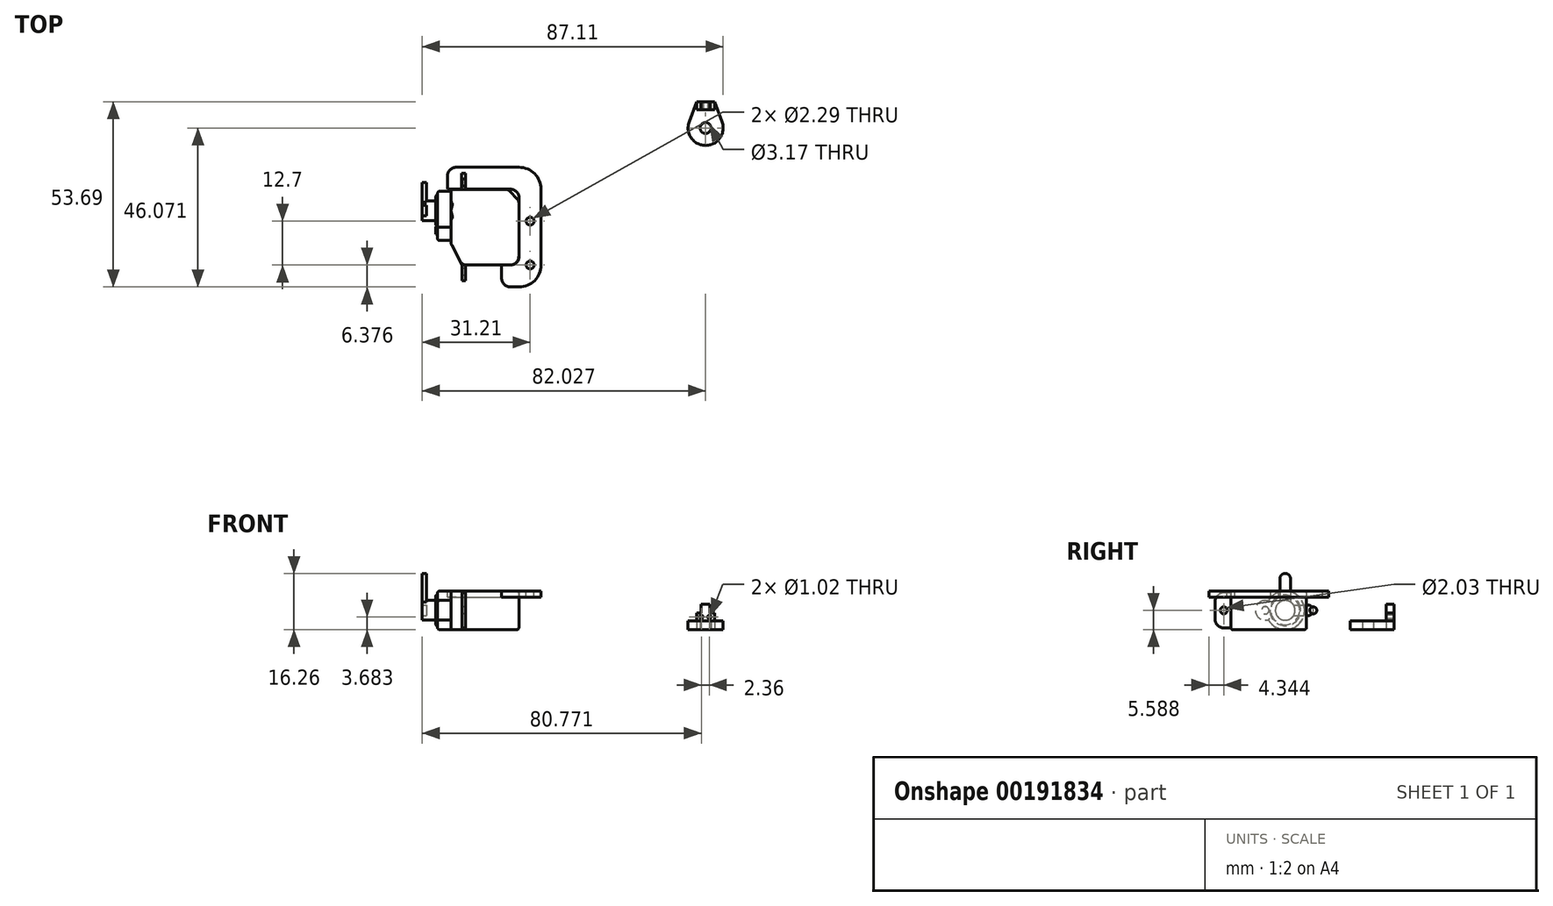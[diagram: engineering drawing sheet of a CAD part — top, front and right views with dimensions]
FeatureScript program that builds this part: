
annotation { "Feature Type Name" : "Feature", "Feature Type Description" : "" }
export const myFeature = defineFeature(function(context is Context, id is Id, definition is map)
    precondition{}
    {
        {
            var Q0;
            Q0=qCreatedBy(makeId("Top.planeOp"),FACE);
            var sketch = newSketch(context, id + "F0", { "sketchPlane" : qUnion([Q0])});
            skLineSegment(sketch, "E0.top", {"start": v(-31.68, -0.42) * mm, "end": v(-18.72, -0.42) * mm});
            skLineSegment(sketch, "E0.left", {"start": v(-35.87, 22.38) * mm, "end": v(-35.87, 6.41) * mm});
            skLineSegment(sketch, "E0.right", {"start": v(-16.18, 17.68) * mm, "end": v(-16.18, 2.12) * mm});
            skLineSegment(sketch, "E1", {"start": v(-32.7, -0.42) * mm, "end": v(-35.59, 5.26) * mm});
            skLineSegment(sketch, "E2.top", {"start": v(-32.7, -5) * mm, "end": v(-31.68, -5) * mm});
            skLineSegment(sketch, "E2.left", {"start": v(-32.7, -0.42) * mm, "end": v(-32.7, -5) * mm});
            skLineSegment(sketch, "E2.right", {"start": v(-31.68, -0.42) * mm, "end": v(-31.68, -5) * mm});
            skPoint(sketch, "E3.visualSharp", {"position": v(-17.03, 21.42) * mm});
            skPoint(sketch, "E4.visualSharp", {"position": v(-16.18, 22.74) * mm});
            skPoint(sketch, "E5.visualSharp", {"position": v(-16.18, -0.42) * mm});
            skArc(sketch, "E5.filletArc", {"start": v(-18.72, -0.42) * mm, "mid": v(-16.93, 0.32) * mm, "end": v(-16.18, 2.12) * mm});
            skPoint(sketch, "E6.visualSharp", {"position": v(-35.87, 5.8) * mm});
            skArc(sketch, "E6.filletArc", {"start": v(-35.87, 6.41) * mm, "mid": v(-35.8, 5.82) * mm, "end": v(-35.59, 5.26) * mm});
            skLineSegment(sketch, "E7", {"start": v(-43.65, 10.5) * mm, "end": v(-4.37, 10.5) * mm, "construction": true});
            skLineSegment(sketch, "E8.MirrorCS", {"start": v(-31.68, 21.42) * mm, "end": v(-31.68, 26) * mm});
            skLineSegment(sketch, "E9.MirrorCS", {"start": v(-32.7, 21.42) * mm, "end": v(-32.7, 26) * mm});
            skLineSegment(sketch, "E10.MirrorCS", {"start": v(-32.7, 26) * mm, "end": v(-31.68, 26) * mm});
            skLineSegment(sketch, "E11.trimOffspring", {"start": v(-31.68, 21.42) * mm, "end": v(-19.8, 21.42) * mm});
            skLineSegment(sketch, "E12", {"start": v(-32.7, 21.42) * mm, "end": v(-33.48, 21.42) * mm});
            skLineSegment(sketch, "E13", {"start": v(-33.48, 21.42) * mm, "end": v(-35.36, 21.42) * mm});
            skLineSegment(sketch, "E14", {"start": v(-35.87, 22.38) * mm, "end": v(-35.87, 20.91) * mm});
            skPoint(sketch, "E15.visualSharp", {"position": v(-35.87, 21.42) * mm});
            skArc(sketch, "E15.filletArc", {"start": v(-35.36, 21.42) * mm, "mid": v(-35.72, 21.27) * mm, "end": v(-35.87, 20.91) * mm});
            skLineSegment(sketch, "E16", {"start": v(-18.88, 21.03) * mm, "end": v(-16.53, 18.56) * mm});
            skPoint(sketch, "E17.visualSharp", {"position": v(-19.26, 21.42) * mm});
            skArc(sketch, "E17.filletArc", {"start": v(-18.88, 21.03) * mm, "mid": v(-19.3, 21.32) * mm, "end": v(-19.8, 21.42) * mm});
            skPoint(sketch, "E18.visualSharp", {"position": v(-16.18, 18.2) * mm});
            skArc(sketch, "E18.filletArc", {"start": v(-16.18, 17.68) * mm, "mid": v(-16.27, 18.15) * mm, "end": v(-16.53, 18.56) * mm});
            skSolve(sketch);
        }
        {
            var Q0;
            Q0=makeQuery(id+"F0.imprint","IMPRINT",FACE,{"disambiguationData":[TD([[makeQuery(id+"F0.imprint","IMPRINT",EDGE,{"derivedFrom":sQuery(id+"F0.wireOp",EDGE,"E0.top")}),1.0]])]});
            extrude(context, id + "F1", {"entities" : qUnion([Q0]), "depth" : 11.18 * mm});
        }
        {
            var Q0;
            Q0=makeQuery(id+"F1.opExtrude","SWEPT_FACE",FACE,{"disambiguationData":[OSD([sQuery(id+"F0.wireOp",EDGE,"E0.left")])]});
            var sketch = newSketch(context, id + "F2", { "sketchPlane" : qUnion([Q0])});
            skArc(sketch, "E19", {"start": v(-10.44, 8.3) * mm, "mid": v(-20.91, 5.59) * mm, "end": v(-10.44, 2.87) * mm});
            skLineSegment(sketch, "E20", {"start": v(-6.41, 5.59) * mm, "end": v(-20.91, 5.59) * mm, "construction": true});
            skArc(sketch, "E21", {"start": v(-10.44, 2.87) * mm, "mid": v(-6.7, 5.59) * mm, "end": v(-10.44, 8.3) * mm});
            skLineSegment(sketch, "E22", {"start": v(-9.55, 2.73) * mm, "end": v(-10.52, 2.73) * mm});
            skLineSegment(sketch, "E23", {"start": v(-9.55, 8.45) * mm, "end": v(-10.52, 8.45) * mm});
            skSolve(sketch);
        }
        {
            var Q0;
            Q0 = qSketchRegion(id + "F2", true);
            extrude(context, id + "F3", {"entities" : qUnion([Q0]), "operationType" : NewBodyOperationType.ADD, "depth" : 3.8 * mm});
        }
        {
            var Q0;
            Q0=makeQuery(id+"F3.opExtrude","CAP_FACE",FACE,{"disambiguationData":[OSD([sQuery(id+"F2.wireOp",EDGE,"E19"),sQuery(id+"F2.wireOp",EDGE,"E21"),sQuery(id+"F2.wireOp",EDGE,"E22"),sQuery(id+"F2.wireOp",EDGE,"E23")])],"isStart":false});
            fillet(context, id + "F4", {"entities" : qUnion([Q0]), "radius" : 0.5 * mm, "tangentPropagation" : true, "allowEdgeOverflow" : false});
        }
        {
            var Q0;
            Q0=makeQuery(id+"F3.opExtrude","CAP_FACE",FACE,{"disambiguationData":[OSD([sQuery(id+"F2.wireOp",EDGE,"E19"),sQuery(id+"F2.wireOp",EDGE,"E21"),sQuery(id+"F2.wireOp",EDGE,"E22"),sQuery(id+"F2.wireOp",EDGE,"E23")])],"isStart":false});
            var sketch = newSketch(context, id + "F5", { "sketchPlane" : qUnion([Q0])});
            skCircle(sketch, "E24", {"center": v(-15.33, 5.59) * mm, "radius": 4.45 * mm});
            skCircle(sketch, "E25", {"center": v(-9.55, 5.59) * mm, "radius": 1.08 * mm});
            skSolve(sketch);
        }
        {
            var Q0;
            Q0 = qSketchRegion(id + "F5", true);
            extrude(context, id + "F6", {"entities" : qUnion([Q0]), "operationType" : NewBodyOperationType.ADD, "depth" : 0.64 * mm});
        }
        {
            var Q0;
            Q0=makeQuery(id+"F6.opExtrude","CAP_FACE",FACE,{"disambiguationData":[OSD([sQuery(id+"F5.wireOp",EDGE,"E24")])],"isStart":false});
            chamfer(context, id + "F7", {"entities" : qUnion([Q0]), "width" : 0.25 * mm, "tangentPropagation" : true});
        }
        {
            var Q0;
            Q0=makeQuery(id+"F1.opExtrude","SWEPT_FACE",FACE,{"disambiguationData":[OSD([sQuery(id+"F0.wireOp",EDGE,"E2.left")])]});
            var sketch = newSketch(context, id + "F8", { "sketchPlane" : qUnion([Q0])});
            skLineSegment(sketch, "E26.bottom", {"start": v(0.42, 0.5) * mm, "end": v(2.46, 0.5) * mm});
            skLineSegment(sketch, "E26.top", {"start": v(0.42, 10.67) * mm, "end": v(2.46, 10.67) * mm});
            skLineSegment(sketch, "E26.left", {"start": v(0.42, 0.5) * mm, "end": v(0.42, 10.67) * mm});
            skLineSegment(sketch, "E26.right", {"start": v(5, 3.05) * mm, "end": v(5, 8.13) * mm});
            skPoint(sketch, "E27.visualSharp", {"position": v(5, 0.5) * mm});
            skArc(sketch, "E27.filletArc", {"start": v(2.46, 0.5) * mm, "mid": v(4.25, 1.25) * mm, "end": v(5, 3.05) * mm});
            skPoint(sketch, "E28.visualSharp", {"position": v(5, 10.67) * mm});
            skArc(sketch, "E28.filletArc", {"start": v(5, 8.13) * mm, "mid": v(4.25, 9.92) * mm, "end": v(2.46, 10.67) * mm});
            skCircle(sketch, "E29", {"center": v(2.46, 5.59) * mm, "radius": 1.02 * mm});
            skLineSegment(sketch, "E30", {"start": v(0.42, 5.59) * mm, "end": v(5, 5.59) * mm, "construction": true});
            skLineSegment(sketch, "E31", {"start": v(-10.5, -16.54) * mm, "end": v(-10.5, 30.53) * mm, "construction": true});
            skLineSegment(sketch, "E32.MirrorCS", {"start": v(-21.42, 10.67) * mm, "end": v(-23.45, 10.67) * mm});
            skLineSegment(sketch, "E33.MirrorCS", {"start": v(-21.42, 0.5) * mm, "end": v(-23.45, 0.5) * mm});
            skArc(sketch, "E34.MirrorCS", {"start": v(-23.45, 0.5) * mm, "mid": v(-25.25, 1.25) * mm, "end": v(-26, 3.05) * mm});
            skLineSegment(sketch, "E35.MirrorCS", {"start": v(-21.42, 5.59) * mm, "end": v(-26, 5.59) * mm, "construction": true});
            skLineSegment(sketch, "E36.MirrorCS", {"start": v(-26, 3.05) * mm, "end": v(-26, 8.13) * mm});
            skArc(sketch, "E37.MirrorCS", {"start": v(-26, 8.13) * mm, "mid": v(-25.25, 9.92) * mm, "end": v(-23.45, 10.67) * mm});
            skCircle(sketch, "E38.MirrorC", {"center": v(-23.45, 5.59) * mm, "radius": 1.02 * mm});
            skPoint(sketch, "E39.MirrorP", {"position": v(-26, 10.67) * mm});
            skLineSegment(sketch, "E40.MirrorCS", {"start": v(-21.42, 0.5) * mm, "end": v(-21.42, 10.67) * mm});
            skPoint(sketch, "E41.MirrorP", {"position": v(-26, 0.5) * mm});
            skLineSegment(sketch, "E42.bottom", {"start": v(-21.42, 0) * mm, "end": v(-26, 0) * mm});
            skLineSegment(sketch, "E42.top", {"start": v(-21.42, 11.2) * mm, "end": v(-26, 11.2) * mm});
            skLineSegment(sketch, "E42.left", {"start": v(-21.42, 0) * mm, "end": v(-21.42, 11.2) * mm});
            skLineSegment(sketch, "E42.right", {"start": v(-26, 0) * mm, "end": v(-26, 11.2) * mm});
            skSolve(sketch);
        }
        {
            var Q0;
            Q0=makeQuery(id+"F8.imprint","IMPRINT",FACE,{"disambiguationData":[TD([[makeQuery(id+"F8.imprint","IMPRINT",EDGE,{"derivedFrom":sQuery(id+"F8.wireOp",EDGE,"E29")}),1.0]])]});
            var Q1;
            {var subQ0=sQuery(id+"F8.wireOp",EDGE,"E28.filletArc");Q1=makeQuery(id+"F8.imprint","IMPRINT",FACE,{"disambiguationData":[TD([[makeQuery(id+"F8.imprint","IMPRINT",EDGE,{"derivedFrom":subQ0}),-1.0]])]});}
            var Q2;
            {var subQ0=sQuery(id+"F8.wireOp",EDGE,"E27.filletArc");Q2=makeQuery(id+"F8.imprint","IMPRINT",FACE,{"disambiguationData":[TD([[makeQuery(id+"F8.imprint","IMPRINT",EDGE,{"derivedFrom":subQ0}),-1.0]])]});}
            var Q3;
            {var subQ1=sQuery(id+"F8.wireOp",EDGE,"E32.MirrorCS");Q3=makeQuery(id+"F8.imprint","IMPRINT",FACE,{"disambiguationData":[TD([[makeQuery(id+"F8.imprint","IMPRINT",EDGE,{"derivedFrom":subQ1}),-1.0]])]});}
            var Q4;
            {var subQ1=sQuery(id+"F8.wireOp",EDGE,"E33.MirrorCS");Q4=makeQuery(id+"F8.imprint","IMPRINT",FACE,{"disambiguationData":[TD([[makeQuery(id+"F8.imprint","IMPRINT",EDGE,{"derivedFrom":subQ1}),1.0]])]});}
            var Q5;
            Q5=makeQuery(id+"F8.imprint","IMPRINT",FACE,{"disambiguationData":[TD([[makeQuery(id+"F8.imprint","IMPRINT",EDGE,{"derivedFrom":sQuery(id+"F8.wireOp",EDGE,"E38.MirrorC")}),-1.0]])]});
            extrude(context, id + "F9", {"entities" : qUnion([Q0, Q1, Q2, Q3, Q4, Q5]), "operationType" : NewBodyOperationType.REMOVE, "endBound" : BoundingType.THROUGH_ALL, "oppositeDirection" : true, "depth" : 25.4 * mm});
        }
        {
            var Q0;
            Q0=makeQuery(id+"F1.opExtrude","CAP_FACE",FACE,{"disambiguationData":[OSD([sQuery(id+"F0.wireOp",EDGE,"E0.top"),sQuery(id+"F0.wireOp",EDGE,"E0.left"),sQuery(id+"F0.wireOp",EDGE,"E0.right"),sQuery(id+"F0.wireOp",EDGE,"0QajpKrW-Zkmi-OHnB-r6oI-nad7adF06jMD"),sQuery(id+"F0.wireOp",EDGE,"E1"),sQuery(id+"F0.wireOp",EDGE,"E2.top"),sQuery(id+"F0.wireOp",EDGE,"E2.left"),sQuery(id+"F0.wireOp",EDGE,"E2.right"),sQuery(id+"F0.wireOp",EDGE,"E3.filletArc"),sQuery(id+"F0.wireOp",EDGE,"E4.filletArc"),sQuery(id+"F0.wireOp",EDGE,"E5.filletArc"),sQuery(id+"F0.wireOp",EDGE,"E6.filletArc"),sQuery(id+"F0.wireOp",EDGE,"E8.MirrorCS"),sQuery(id+"F0.wireOp",EDGE,"E9.MirrorCS"),sQuery(id+"F0.wireOp",EDGE,"E10.MirrorCS"),sQuery(id+"F0.wireOp",EDGE,"E11.trimOffspring"),sQuery(id+"F0.wireOp",EDGE,"E12"),sQuery(id+"F0.wireOp",EDGE,"E13"),sQuery(id+"F0.wireOp",EDGE,"E14"),sQuery(id+"F0.wireOp",EDGE,"E15.filletArc")])],"isStart":false});
            var Q1;
            Q1=makeQuery(id+"F1.opExtrude","CAP_FACE",FACE,{"disambiguationData":[OSD([sQuery(id+"F0.wireOp",EDGE,"E0.top"),sQuery(id+"F0.wireOp",EDGE,"E0.left"),sQuery(id+"F0.wireOp",EDGE,"E0.right"),sQuery(id+"F0.wireOp",EDGE,"0QajpKrW-Zkmi-OHnB-r6oI-nad7adF06jMD"),sQuery(id+"F0.wireOp",EDGE,"E1"),sQuery(id+"F0.wireOp",EDGE,"E2.top"),sQuery(id+"F0.wireOp",EDGE,"E2.left"),sQuery(id+"F0.wireOp",EDGE,"E2.right"),sQuery(id+"F0.wireOp",EDGE,"E3.filletArc"),sQuery(id+"F0.wireOp",EDGE,"E4.filletArc"),sQuery(id+"F0.wireOp",EDGE,"E5.filletArc"),sQuery(id+"F0.wireOp",EDGE,"E6.filletArc"),sQuery(id+"F0.wireOp",EDGE,"E8.MirrorCS"),sQuery(id+"F0.wireOp",EDGE,"E9.MirrorCS"),sQuery(id+"F0.wireOp",EDGE,"E10.MirrorCS"),sQuery(id+"F0.wireOp",EDGE,"E11.trimOffspring"),sQuery(id+"F0.wireOp",EDGE,"E12"),sQuery(id+"F0.wireOp",EDGE,"E13"),sQuery(id+"F0.wireOp",EDGE,"E14"),sQuery(id+"F0.wireOp",EDGE,"E15.filletArc")])],"isStart":true});
            fillet(context, id + "F10", {"entities" : qUnion([Q0, Q1]), "radius" : 0.5 * mm, "tangentPropagation" : true, "allowEdgeOverflow" : false});
        }
        {
            var Q0;
            Q0=makeQuery(id+"F6.opExtrude","CAP_FACE",FACE,{"disambiguationData":[OSD([sQuery(id+"F5.wireOp",EDGE,"E24")])],"isStart":false});
            var sketch = newSketch(context, id + "F11", { "sketchPlane" : qUnion([Q0])});
            skCircle(sketch, "E43", {"center": v(-15.33, 5.59) * mm, "radius": 2.86 * mm});
            skSolve(sketch);
        }
        {
            var Q0;
            Q0 = qSketchRegion(id + "F11", true);
            extrude(context, id + "F12", {"entities" : qUnion([Q0]), "depth" : 3.8 * mm});
        }
        {
            var Q0;
            Q0=qCreatedBy(makeId("Top.planeOp"),FACE);
            var sketch = newSketch(context, id + "F13", { "sketchPlane" : qUnion([Q0])});
            skArc(sketch, "E44", {"start": v(33.13, 41) * mm, "mid": v(37.9, 34.2) * mm, "end": v(42.68, 41) * mm});
            skLineSegment(sketch, "E45", {"start": v(33.13, 41) * mm, "end": v(35.27, 46.9) * mm});
            skLineSegment(sketch, "E46", {"start": v(35.27, 46.9) * mm, "end": v(36.64, 46.9) * mm});
            skLineSegment(sketch, "E47", {"start": v(40.54, 46.9) * mm, "end": v(42.68, 41) * mm});
            skCircle(sketch, "E48", {"center": v(37.9, 39.27) * mm, "radius": 1.59 * mm});
            skLineSegment(sketch, "E49", {"start": v(37.9, 39.27) * mm, "end": v(37.9, 46.9) * mm, "construction": true});
            skLineSegment(sketch, "E50.top", {"start": v(36.64, 44.6) * mm, "end": v(39.18, 44.6) * mm});
            skLineSegment(sketch, "E50.left", {"start": v(36.64, 46.9) * mm, "end": v(36.64, 44.6) * mm});
            skLineSegment(sketch, "E50.right", {"start": v(39.18, 46.9) * mm, "end": v(39.18, 44.6) * mm});
            skLineSegment(sketch, "E51.trimOffspring", {"start": v(39.18, 46.9) * mm, "end": v(40.54, 46.9) * mm});
            skSolve(sketch);
        }
        {
            var Q0;
            Q0=makeQuery(id+"F12.opExtrude","CAP_FACE",FACE,{"disambiguationData":[OSD([sQuery(id+"F11.wireOp",EDGE,"E43")])],"isStart":false});
            var sketch = newSketch(context, id + "F14", { "sketchPlane" : qUnion([Q0])});
            skLineSegment(sketch, "E52.right", {"start": v(-7.2, 5.59) * mm, "end": v(-7.2, 5.59) * mm});
            skPoint(sketch, "E52.middle", {"position": v(-15.33, 5.59) * mm});
            skLineSegment(sketch, "E53.bottom", {"start": v(-15.33, 16.26) * mm, "end": v(-15.33, 16.26) * mm});
            skLineSegment(sketch, "E53.left", {"start": v(-16.85, 14.73) * mm, "end": v(-16.85, 7.11) * mm});
            skLineSegment(sketch, "E53.right", {"start": v(-13.8, 14.73) * mm, "end": v(-13.8, 7.11) * mm});
            skPoint(sketch, "E54.visualSharp", {"position": v(-16.85, 16.26) * mm});
            skArc(sketch, "E54.filletArc", {"start": v(-15.33, 16.26) * mm, "mid": v(-16.4, 15.8) * mm, "end": v(-16.85, 14.73) * mm});
            skPoint(sketch, "E55.visualSharp", {"position": v(-13.8, 16.26) * mm});
            skArc(sketch, "E55.filletArc", {"start": v(-13.8, 14.73) * mm, "mid": v(-14.25, 15.8) * mm, "end": v(-15.33, 16.26) * mm});
            skPoint(sketch, "E56.visualSharp", {"position": v(-7.2, 7.11) * mm});
            skPoint(sketch, "E57.visualSharp", {"position": v(-7.2, 4.06) * mm});
            skLineSegment(sketch, "E58", {"start": v(-15.33, 16.26) * mm, "end": v(-15.33, -4.57) * mm, "construction": true});
            skLineSegment(sketch, "E59.MirrorCS", {"start": v(-16.85, 7.11) * mm, "end": v(-21.93, 7.11) * mm});
            skArc(sketch, "E60.MirrorCS", {"start": v(-23.45, 5.59) * mm, "mid": v(-23, 6.67) * mm, "end": v(-21.93, 7.11) * mm});
            skArc(sketch, "E61.MirrorCS", {"start": v(-21.93, 4.06) * mm, "mid": v(-23, 4.51) * mm, "end": v(-23.45, 5.59) * mm});
            skLineSegment(sketch, "E62.MirrorCS", {"start": v(-16.85, 4.06) * mm, "end": v(-21.93, 4.06) * mm});
            skLineSegment(sketch, "E63.MirrorCS", {"start": v(-13.8, 7.11) * mm, "end": v(-16.85, 4.06) * mm});
            skPoint(sketch, "E64.trimOffspring.start.orphan", {"position": v(-13.8, 4.06) * mm});
            skPoint(sketch, "E57.filletArc.start.orphan", {"position": v(-8.72, 4.06) * mm});
            skPoint(sketch, "E56.filletArc.end.orphan", {"position": v(-8.72, 7.11) * mm});
            skSolve(sketch);
        }
        {
            var Q0;
            Q0 = qSketchRegion(id + "F14", true);
            extrude(context, id + "F15", {"entities" : qUnion([Q0]), "operationType" : NewBodyOperationType.ADD, "oppositeDirection" : true, "depth" : 1.27 * mm});
        }
        {
            var Q0;
            Q0 = qSketchRegion(id + "F13", true);
            extrude(context, id + "F16", {"entities" : qUnion([Q0]), "depth" : 2.54 * mm});
        }
        {
            var Q0;
            Q0=makeQuery(id+"F1.opExtrude","CAP_FACE",FACE,{"disambiguationData":[OSD([sQuery(id+"F0.wireOp",EDGE,"E0.top"),sQuery(id+"F0.wireOp",EDGE,"E0.left"),sQuery(id+"F0.wireOp",EDGE,"E0.right"),sQuery(id+"F0.wireOp",EDGE,"E1"),sQuery(id+"F0.wireOp",EDGE,"E2.top"),sQuery(id+"F0.wireOp",EDGE,"E2.left"),sQuery(id+"F0.wireOp",EDGE,"E2.right"),sQuery(id+"F0.wireOp",EDGE,"E5.filletArc"),sQuery(id+"F0.wireOp",EDGE,"E6.filletArc"),sQuery(id+"F0.wireOp",EDGE,"E8.MirrorCS"),sQuery(id+"F0.wireOp",EDGE,"E9.MirrorCS"),sQuery(id+"F0.wireOp",EDGE,"E10.MirrorCS"),sQuery(id+"F0.wireOp",EDGE,"E11.trimOffspring"),sQuery(id+"F0.wireOp",EDGE,"E12"),sQuery(id+"F0.wireOp",EDGE,"E13"),sQuery(id+"F0.wireOp",EDGE,"E15.filletArc"),sQuery(id+"F0.wireOp",EDGE,"E16"),sQuery(id+"F0.wireOp",EDGE,"E17.filletArc"),sQuery(id+"F0.wireOp",EDGE,"E18.filletArc")])],"isStart":false});
            var sketch = newSketch(context, id + "F17", { "sketchPlane" : qUnion([Q0])});
            skLineSegment(sketch, "E65.bottom", {"start": v(-34.3, 27.87) * mm, "end": v(-16.08, 27.87) * mm});
            skLineSegment(sketch, "E65.top", {"start": v(-18.62, -6.8) * mm, "end": v(-16.08, -6.8) * mm});
            skLineSegment(sketch, "E65.left", {"start": v(-36.84, 25.33) * mm, "end": v(-36.84, 21.52) * mm});
            skLineSegment(sketch, "E65.right", {"start": v(-9.73, 21.52) * mm, "end": v(-9.73, -0.45) * mm});
            skLineSegment(sketch, "E66.bottom", {"start": v(-36.84, 21.52) * mm, "end": v(-32.7, 21.52) * mm});
            skLineSegment(sketch, "E66.top", {"start": v(-21.16, -0.45) * mm, "end": v(-18.62, -0.45) * mm});
            skLineSegment(sketch, "E66.right", {"start": v(-16.08, 18.98) * mm, "end": v(-16.08, 2.09) * mm});
            skLineSegment(sketch, "E67.top", {"start": v(-32.7, 26.1) * mm, "end": v(-31.58, 26.1) * mm});
            skLineSegment(sketch, "E67.left", {"start": v(-32.7, 21.52) * mm, "end": v(-32.7, 26.1) * mm});
            skLineSegment(sketch, "E67.right", {"start": v(-31.58, 21.52) * mm, "end": v(-31.58, 26.1) * mm});
            skLineSegment(sketch, "E68.trimOffspring", {"start": v(-31.58, 21.52) * mm, "end": v(-18.62, 21.52) * mm});
            skLineSegment(sketch, "E69.right", {"start": v(-21.16, -0.45) * mm, "end": v(-21.16, -4.26) * mm});
            skPoint(sketch, "E70.visualSharp", {"position": v(-9.73, 27.87) * mm});
            skArc(sketch, "E70.filletArc", {"start": v(-9.73, 21.52) * mm, "mid": v(-11.6, 26) * mm, "end": v(-16.08, 27.87) * mm});
            skPoint(sketch, "E71.visualSharp", {"position": v(-9.73, -6.8) * mm});
            skArc(sketch, "E71.filletArc", {"start": v(-16.08, -6.8) * mm, "mid": v(-11.6, -4.94) * mm, "end": v(-9.73, -0.45) * mm});
            skPoint(sketch, "E72.visualSharp", {"position": v(-36.84, 27.87) * mm});
            skArc(sketch, "E72.filletArc", {"start": v(-34.3, 27.87) * mm, "mid": v(-36.1, 27.13) * mm, "end": v(-36.84, 25.33) * mm});
            skArc(sketch, "E73.filletArc", {"start": v(-16.08, 18.98) * mm, "mid": v(-16.83, 20.78) * mm, "end": v(-18.62, 21.52) * mm});
            skLineSegment(sketch, "E74.filletArc", {"start": v(-16.08, -0.45) * mm, "end": v(-16.08, -0.45) * mm});
            skArc(sketch, "E75.filletArc", {"start": v(-18.62, -0.45) * mm, "mid": v(-16.83, 0.3) * mm, "end": v(-16.08, 2.09) * mm});
            skPoint(sketch, "E76.visualSharp", {"position": v(-21.16, -6.8) * mm});
            skArc(sketch, "E76.filletArc", {"start": v(-21.16, -4.26) * mm, "mid": v(-20.42, -6.06) * mm, "end": v(-18.62, -6.8) * mm});
            skCircle(sketch, "E77", {"center": v(-12.9, 12.28) * mm, "radius": 1.14 * mm});
            skCircle(sketch, "E78", {"center": v(-12.9, -0.42) * mm, "radius": 1.14 * mm});
            skSolve(sketch);
        }
        {
            var Q0;
            Q0 = qSketchRegion(id + "F17", true);
            extrude(context, id + "F18", {"entities" : qUnion([Q0]), "oppositeDirection" : true, "depth" : 1.78 * mm});
        }
        {
            var Q0;
            Q0=makeQuery(id+"F16.opExtrude","SWEPT_FACE",FACE,{"disambiguationData":[OSD([sQuery(id+"F13.wireOp",EDGE,"E50.top")])]});
            var sketch = newSketch(context, id + "F19", { "sketchPlane" : qUnion([Q0])});
            skLineSegment(sketch, "E79.bottom", {"start": v(-36.64, 0) * mm, "end": v(-39.18, 0) * mm});
            skLineSegment(sketch, "E79.left", {"start": v(-36.64, 0) * mm, "end": v(-36.64, 2.54) * mm});
            skLineSegment(sketch, "E79.right", {"start": v(-39.18, 0) * mm, "end": v(-39.18, 2.54) * mm});
            skLineSegment(sketch, "E80.top", {"start": v(-35.25, 4.83) * mm, "end": v(-36.64, 4.83) * mm});
            skLineSegment(sketch, "E80.left", {"start": v(-35.25, 2.54) * mm, "end": v(-35.25, 4.83) * mm});
            skLineSegment(sketch, "E80.right", {"start": v(-40.54, 2.54) * mm, "end": v(-40.54, 4.83) * mm});
            skLineSegment(sketch, "E81", {"start": v(-35.25, 3.68) * mm, "end": v(-40.54, 3.68) * mm, "construction": true});
            skLineSegment(sketch, "E82.trimOffspring", {"start": v(-39.18, 2.54) * mm, "end": v(-40.54, 2.54) * mm});
            skLineSegment(sketch, "E83.MirrorCS", {"start": v(-36.64, 7.37) * mm, "end": v(-36.64, 4.83) * mm});
            skLineSegment(sketch, "E84.MirrorCS", {"start": v(-36.64, 7.37) * mm, "end": v(-39.18, 7.37) * mm});
            skLineSegment(sketch, "E85.MirrorCS", {"start": v(-39.18, 7.37) * mm, "end": v(-39.18, 4.83) * mm});
            skLineSegment(sketch, "E86.trimOffspring", {"start": v(-39.18, 4.83) * mm, "end": v(-40.54, 4.83) * mm});
            skLineSegment(sketch, "E87", {"start": v(-35.25, 2.54) * mm, "end": v(-36.64, 2.54) * mm});
            skCircle(sketch, "E88", {"center": v(-36.65, 3.68) * mm, "radius": 0.5 * mm});
            skCircle(sketch, "E89", {"center": v(-39.01, 3.68) * mm, "radius": 0.5 * mm});
            skSolve(sketch);
        }
        {
            var Q0;
            Q0 = qSketchRegion(id + "F19", true);
            extrude(context, id + "F20", {"entities" : qUnion([Q0]), "depth" : 2.3 * mm});
        }
    });
